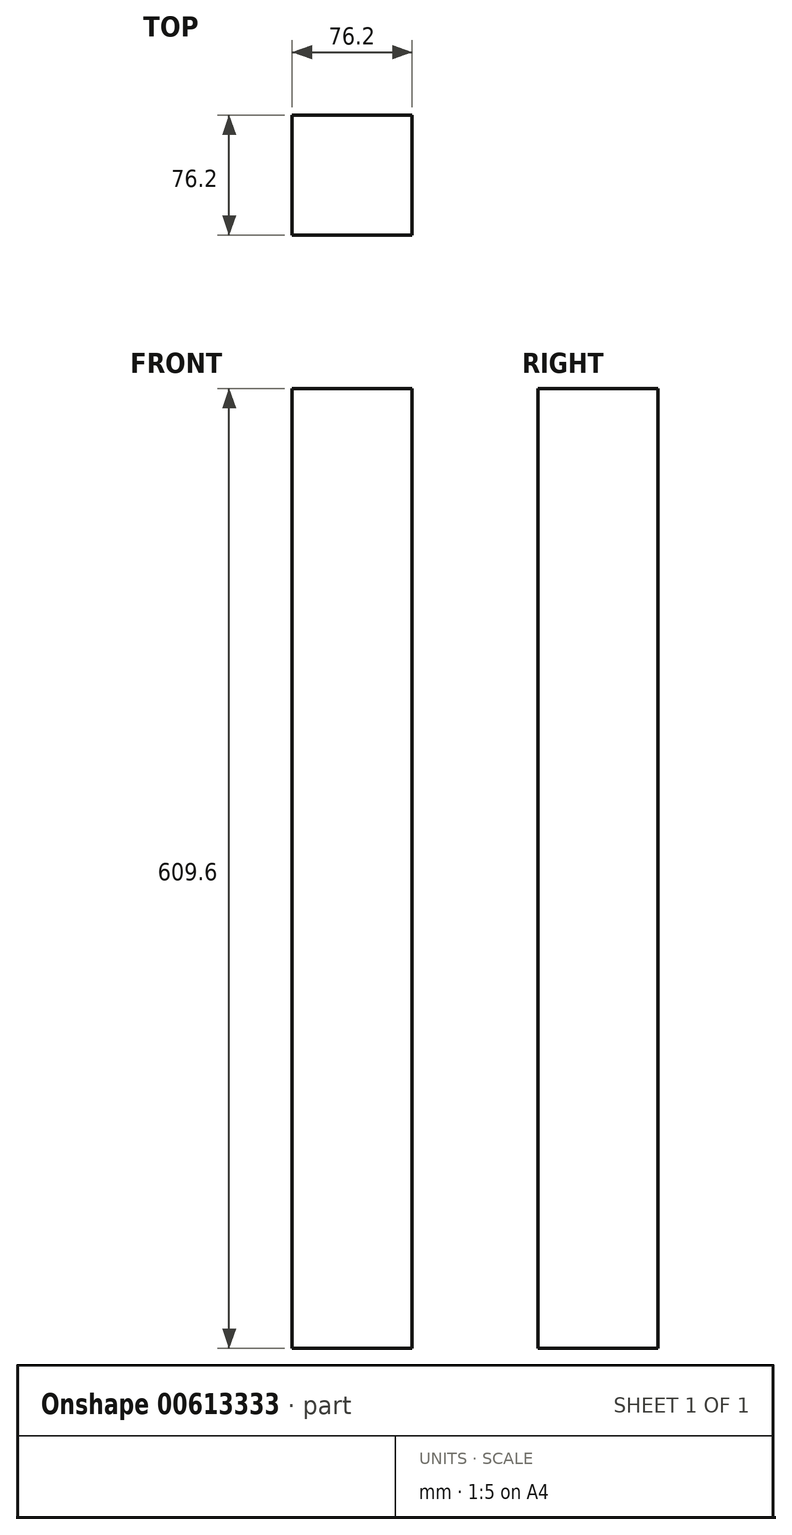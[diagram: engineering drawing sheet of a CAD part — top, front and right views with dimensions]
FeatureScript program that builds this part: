
annotation { "Feature Type Name" : "Feature", "Feature Type Description" : "" }
export const myFeature = defineFeature(function(context is Context, id is Id, definition is map)
    precondition{}
    {
        {
            var Q0;
            Q0=qCreatedBy(makeId("Top.planeOp"),FACE);
            var sketch = newSketch(context, id + "F0", { "sketchPlane" : qUnion([Q0])});
            skLineSegment(sketch, "E0.bottom", {"start": v(38.1, 38.1) * mm, "end": v(-38.1, 38.1) * mm});
            skLineSegment(sketch, "E0.top", {"start": v(38.1, -38.1) * mm, "end": v(-38.1, -38.1) * mm});
            skLineSegment(sketch, "E0.left", {"start": v(38.1, 38.1) * mm, "end": v(38.1, -38.1) * mm});
            skLineSegment(sketch, "E0.right", {"start": v(-38.1, 38.1) * mm, "end": v(-38.1, -38.1) * mm});
            skPoint(sketch, "E0.middle", {"position": v(0, 0) * mm});
            skSolve(sketch);
        }
        {
            var Q0;
            Q0 = qSketchRegion(id + "F0", true);
            extrude(context, id + "F1", {"entities" : qUnion([Q0]), "depth" : 609.6 * mm, "offsetDistance" : 25.4 * mm});
        }
    });
